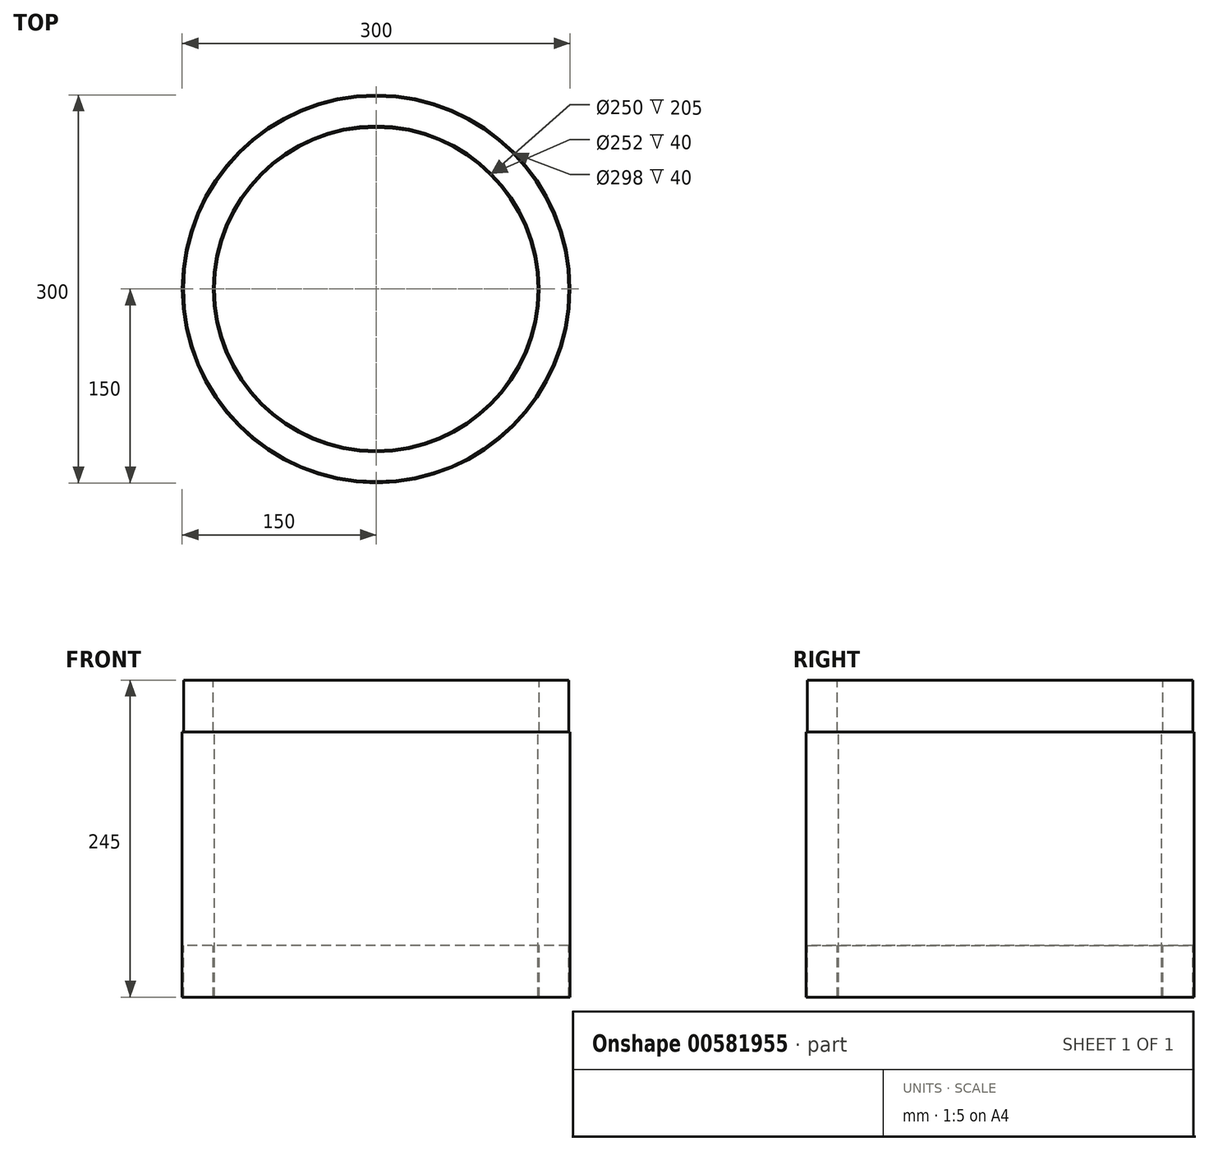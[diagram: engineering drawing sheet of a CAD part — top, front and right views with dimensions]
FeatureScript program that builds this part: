
annotation { "Feature Type Name" : "Feature", "Feature Type Description" : "" }
export const myFeature = defineFeature(function(context is Context, id is Id, definition is map)
    precondition{}
    {
        {
            var Q0;
            Q0=qCreatedBy(makeId("Front.planeOp"),FACE);
            var sketch = newSketch(context, id + "F0", { "sketchPlane" : qUnion([Q0])});
            skLineSegment(sketch, "E0", {"start": v(0, 345.75) * mm, "end": v(0, -558.03) * mm, "construction": true});
            skLineSegment(sketch, "E1", {"start": v(-125, -518.84) * mm, "end": v(-125, -313.84) * mm});
            skLineSegment(sketch, "E2", {"start": v(-125, -313.84) * mm, "end": v(-126, -313.84) * mm});
            skLineSegment(sketch, "E3", {"start": v(-126, -313.84) * mm, "end": v(-126, -273.84) * mm});
            skLineSegment(sketch, "E4", {"start": v(-126, -273.84) * mm, "end": v(-149, -273.84) * mm});
            skLineSegment(sketch, "E5", {"start": v(-149, -273.84) * mm, "end": v(-149, -313.84) * mm});
            skLineSegment(sketch, "E6", {"start": v(-149, -313.84) * mm, "end": v(-150, -313.84) * mm});
            skLineSegment(sketch, "E7", {"start": v(-150, -313.84) * mm, "end": v(-150, -518.84) * mm});
            skLineSegment(sketch, "E8", {"start": v(-150, -518.84) * mm, "end": v(-149, -518.84) * mm});
            skLineSegment(sketch, "E9", {"start": v(-149, -518.84) * mm, "end": v(-149, -478.84) * mm});
            skLineSegment(sketch, "E10", {"start": v(-149, -478.84) * mm, "end": v(-126, -478.84) * mm});
            skLineSegment(sketch, "E11", {"start": v(-126, -478.84) * mm, "end": v(-126, -518.84) * mm});
            skLineSegment(sketch, "E12", {"start": v(-126, -518.84) * mm, "end": v(-125, -518.84) * mm});
            skSolve(sketch);
        }
        {
            var Q0;
            Q0=qSketchRegion(id+"F0",true);
            var Q1;
            Q1=sQuery(id+"F0.wireOp",EDGE,"E0");
            revolve(context, id + "F1", {"entities" : qUnion([Q0]), "axis" : qUnion([Q1]), "revolveType" : RevolveType.FULL});
        }
    });
